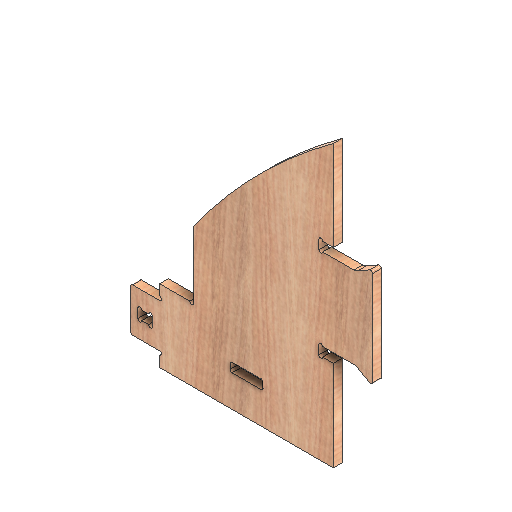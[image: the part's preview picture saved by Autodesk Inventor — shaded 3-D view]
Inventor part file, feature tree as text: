
AUTODESK INVENTOR PART (.ipt)
format: ipt  version: 2021 (Build 250183000, 183)  size: 449,024 bytes
history: native  units: mm
features: other x2, extrude x2, sketch x1, hole x1
ambient origin geometry x8: Origin, YZ Plane, XZ Plane, XY Plane, X Axis, Y Axis, Z Axis, Center Point
bodies: Solid1 (feature_tree)
feature tree (6):
  sketch  "Sketch1"  dims[d53=18.999997mm d55=30.0mm d63=68.0mm d71=30.0mm d75=19.0mm d90=18.0mm d91=0.0mm d92=18.0mm d93=0.0mm]
  other  "CONTOURS"
  hole  "HOLES"  [1 undecoded]
  other  "LETTERS"
  extrude  "Extrusion1"  Depth=68.0mm
  extrude  "Extrusion2"  Depth=30.0mm
note: 1 required parameter value undecoded (feature->parameter linkage not recoverable at this tier; creation-order binding heuristic only, values carry confidence <= 0.55)
